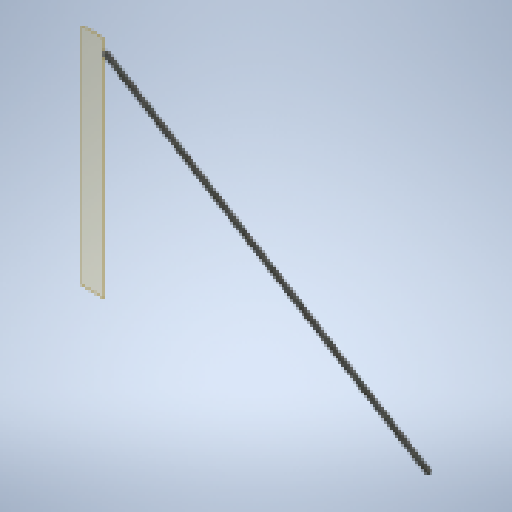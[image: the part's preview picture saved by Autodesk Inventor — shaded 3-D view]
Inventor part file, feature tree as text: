
AUTODESK INVENTOR PART (.ipt)
format: ipt  version: 2025 (Build 290162000, 162)  size: 137,728 bytes
history: native  units: in
note: dims shown in document units (in); Inventor stores cm internally (conversion verified against a paired STEP export)
features: other x3, plane x1, revolve x1, sketch x1
ambient origin geometry x8: Origin, YZ Plane, XZ Plane, XY Plane, X Axis, Y Axis, Z Axis, Center Point
bodies: Solid1 (feature_tree)
feature tree (6):
  plane  "Work Plane1"
  revolve  "Revolution1"  Angle=90.0deg
  sketch  "Sketch1"  dims[d2=0.5in d3=90.0deg]
  other  "<userpath>\OneDrive\Documents\TigerBurn\USCTigerBurn24\v1\Tiger.iam"
  other  "Tiger.iam"
  other  "4x4x40:14"
